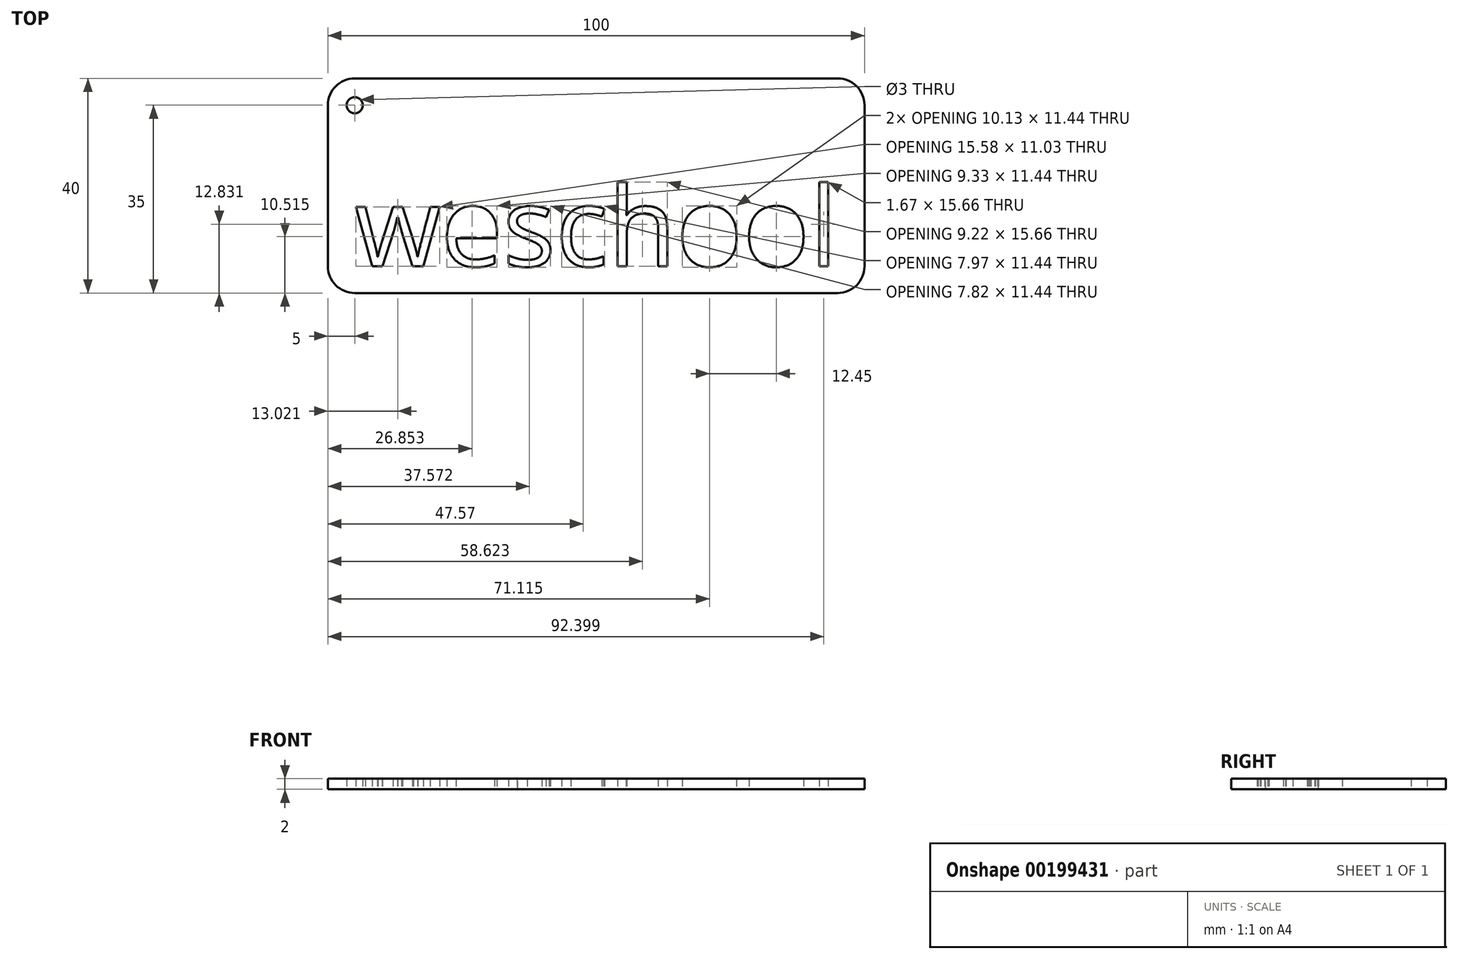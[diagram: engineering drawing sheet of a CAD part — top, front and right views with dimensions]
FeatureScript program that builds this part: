
annotation { "Feature Type Name" : "Feature", "Feature Type Description" : "" }
export const myFeature = defineFeature(function(context is Context, id is Id, definition is map)
    precondition{}
    {
        {
            var Q0;
            Q0=qCreatedBy(makeId("Top.planeOp"),FACE);
            var sketch = newSketch(context, id + "F0", { "sketchPlane" : qUnion([Q0])});
            skLineSegment(sketch, "E0.bottom", {"start": v(5, 0) * mm, "end": v(95, 0) * mm});
            skLineSegment(sketch, "E0.top", {"start": v(5, 40) * mm, "end": v(95, 40) * mm});
            skLineSegment(sketch, "E0.left", {"start": v(0, 5) * mm, "end": v(0, 35) * mm});
            skLineSegment(sketch, "E0.right", {"start": v(100, 5) * mm, "end": v(100, 35) * mm});
            skPoint(sketch, "E1.visualSharp", {"position": v(0, 40) * mm});
            skArc(sketch, "E1.filletArc", {"start": v(5, 40) * mm, "mid": v(1.46, 38.54) * mm, "end": v(0, 35) * mm});
            skPoint(sketch, "E2.visualSharp", {"position": v(0, 0) * mm});
            skArc(sketch, "E2.filletArc", {"start": v(0, 5) * mm, "mid": v(1.46, 1.46) * mm, "end": v(5, 0) * mm});
            skPoint(sketch, "E3.visualSharp", {"position": v(100, 0) * mm});
            skArc(sketch, "E3.filletArc", {"start": v(95, 0) * mm, "mid": v(98.54, 1.46) * mm, "end": v(100, 5) * mm});
            skPoint(sketch, "E4.visualSharp", {"position": v(100, 40) * mm});
            skArc(sketch, "E4.filletArc", {"start": v(100, 35) * mm, "mid": v(98.54, 38.54) * mm, "end": v(95, 40) * mm});
            skCircle(sketch, "E5", {"center": v(5, 35) * mm, "radius": 1.5 * mm});
            skText(sketch, "E6", { "text": "weschool", "fontName": "OpenSans-Regular.ttf"});
            const initialGuessF0  = {"E6": [0.005, 0.005, 1, 0, 0.01484]};
            skSetInitialGuess(sketch, initialGuessF0);
            skSolve(sketch);
        }
        {
            var Q0;
            Q0 = qSketchRegion(id + "F0", true);
            extrude(context, id + "F1", {"entities" : qUnion([Q0]), "depth" : 2 * mm});
        }
    });
